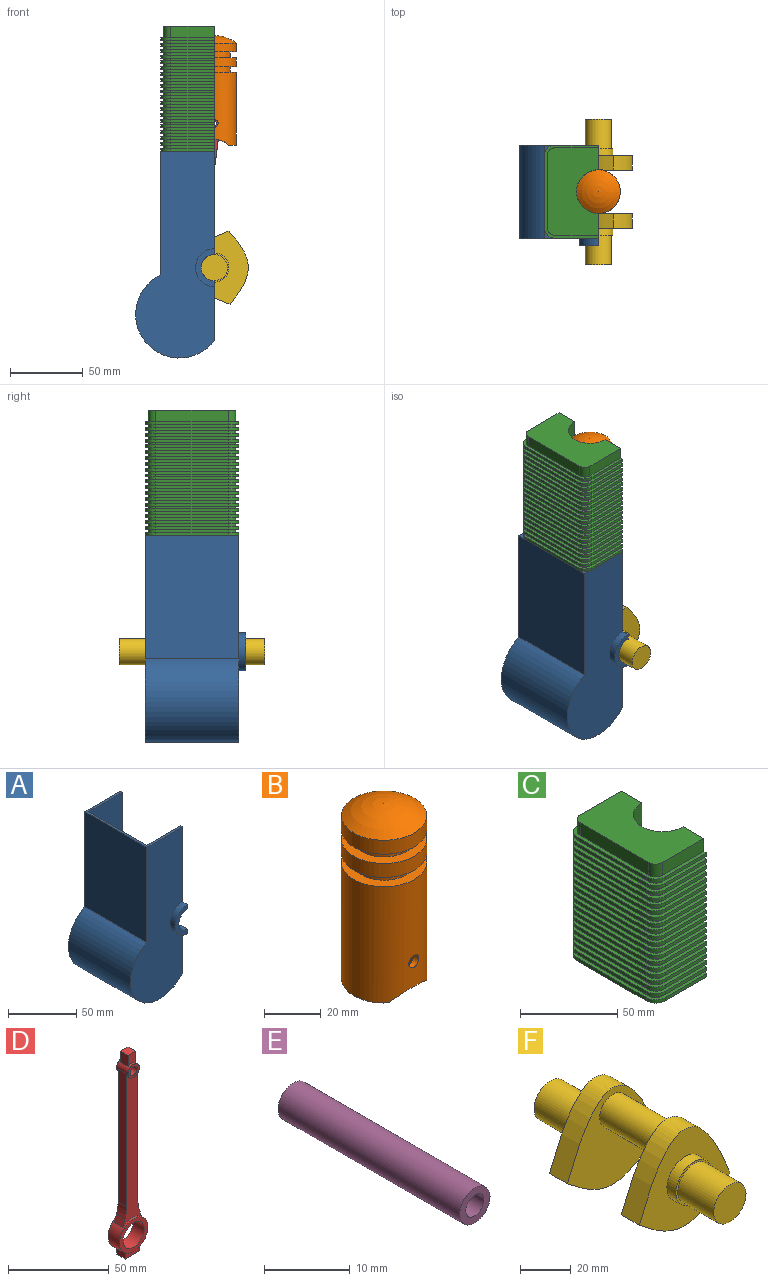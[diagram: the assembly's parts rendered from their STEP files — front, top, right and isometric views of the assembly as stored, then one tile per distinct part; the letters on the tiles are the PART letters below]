
ASSEMBLY  parts=6 mates=4
PART A: 16 faces, bbox 54.1x69x142.1 mm
  f0: plane 71x2mm, normal (1,0,0), area 142mm2, adj f2,f7,f11,f12
  f1: plane 71x7mm, normal (1,0,0), area 162mm2, adj f2,f6,f10,f13,f14,f15
  f2: plane 64x37mm, normal (0,0,1), area 268mm2, adj f0,f1,f5,f6,f7,f9,f10,f11
  f3: plane 69x41mm, normal (1,0,0), area 400.2mm2, adj f4,f6,f7,f8,f10,f11,f12,f13
  f4: cylinder r=30mm len=64mm, axis (0,1,0), area 6965.7mm2, adj f3,f5,f6,f7
  f5: plane 85.03x64mm, normal (-1,0,0), area 5441.9mm2, adj f2,f4,f6,f7
  f6: plane 142.11x54.08mm, normal (0,-1,0), area 5555.5mm2, adj f1,f2,f3,f4,f5,f14
  f7: plane 142.11x54.08mm, normal (0,1,0), area 5693.7mm2, adj f0,f2,f3,f4,f5,f12
  f8: cylinder r=28mm len=60mm, axis (0,1,0), area 6343.8mm2, adj f3,f9,f10,f11
  f9: plane 86.32x60mm, normal (1,0,0), area 5179.4mm2, adj f2,f8,f10,f11
  f10: plane 140.11x52.08mm, normal (0,1,0), area 5307.9mm2, adj f1,f2,f3,f8,f9,f13
  f11: plane 140.11x52.08mm, normal (0,-1,0), area 5307.9mm2, adj f0,f2,f3,f8,f9,f12
  f12: cylinder r=9mm len=18mm, axis (0,-1,0), area 56.5mm2, adj f0,f3,f7,f11
  f13: cylinder r=9mm len=18mm, axis (0,-1,0), area 197.9mm2, adj f1,f3,f10,f15
  f14: cylinder r=13mm len=26mm, axis (0,1,0), area 204.2mm2, adj f1,f3,f6,f15
  f15: plane 26x13mm, normal (0,-1,0), area 138.2mm2, adj f1,f3,f13,f14
PART B: 26 faces, bbox 30x30x75.2 mm
  f0: plane 23.31x5.56mm, normal (0,0,-1), area 55.9mm2, adj f1,f2,f24,f25
  f1: cylinder r=15mm len=50mm, axis (0,0,1), area 4562mm2, adj f0,f3,f4,f22,f23,f24,f25
  f2: cylinder r=12.5mm len=47.5mm, axis (0,0,1), area 3577.3mm2, adj f0,f4,f13,f22,f23,f24,f25
  f3: plane 30x30mm, normal (0,0,1), area 326.7mm2, adj f1,f12
  f4: plane 23.31x5.56mm, normal (0,0,-1), area 55.9mm2, adj f1,f2,f24,f25
  f5: sphere r=24.12mm, area 792.9mm2, adj f6
  f6: cylinder r=15mm len=30mm, axis (0,0,1), area 565.5mm2, adj f5,f7
  f7: plane 30x30mm, normal (0,0,-1), area 326.7mm2, adj f6,f8
  f8: cylinder r=11mm len=22mm, axis (0,0,1), area 276.5mm2, adj f7,f9
  f9: plane 30x30mm, normal (0,0,1), area 326.7mm2, adj f8,f10
  f10: cylinder r=15mm len=30mm, axis (0,0,1), area 565.5mm2, adj f9,f11
  f11: plane 30x30mm, normal (0,0,-1), area 326.7mm2, adj f10,f12
  f12: cylinder r=11mm len=22mm, axis (0,0,1), area 276.5mm2, adj f3,f11
  f13: plane 25x25mm, normal (0,0,-1), area 263.9mm2, adj f2,f21
  f14: sphere r=21.62mm, area 540.7mm2, adj f15
  f15: cylinder r=12.5mm len=25mm, axis (0,0,1), area 176.9mm2, adj f14,f16
  f16: plane 25x25mm, normal (0,0,1), area 263.9mm2, adj f15,f17
  f17: cylinder r=8.5mm len=17mm, axis (0,0,1), area 480.7mm2, adj f16,f18
  f18: plane 25x25mm, normal (0,0,-1), area 263.9mm2, adj f17,f19
  f19: cylinder r=12.5mm len=25mm, axis (0,0,1), area 78.5mm2, adj f18,f20
  f20: plane 25x25mm, normal (0,0,1), area 263.9mm2, adj f19,f21
  f21: cylinder r=8.5mm len=17mm, axis (0,0,1), area 480.7mm2, adj f13,f20
  f22: cylinder r=2.5mm len=5mm, axis (0,1,0), area 39.6mm2, adj f1,f2
  f23: cylinder r=2.5mm len=5mm, axis (0,1,0), area 39.6mm2, adj f1,f2
  f24: cylinder r=13mm len=18.89mm, axis (0,-1,0), area 59mm2, adj f0,f1,f2,f4
  f25: cylinder r=13mm len=18.89mm, axis (0,-1,0), area 59mm2, adj f0,f1,f2,f4
PART C: 244 faces, bbox 37x64x86 mm
  f0: cylinder r=15mm len=86mm, axis (0,0,-1), area 4052.7mm2, adj f1,f7,f8,f231
  f1: plane 86x17mm, normal (1,0,0), area 1370mm2, adj f0,f2,f8,f10,f14,f15,f16,f22
  f2: plane 30x2mm, normal (0,1,0), area 60mm2, adj f1,f3,f14,f237
  f3: cylinder r=5mm len=5mm, axis (0,0,-1), area 15.7mm2, adj f2,f4,f14,f237
  f4: plane 50x2mm, normal (-1,0,0), area 100mm2, adj f3,f5,f14,f237
  f5: cylinder r=5mm len=5mm, axis (0,0,-1), area 15.7mm2, adj f4,f6,f14,f237
  f6: plane 30x2mm, normal (0,-1,0), area 60mm2, adj f5,f7,f14,f237
  f7: plane 86x17mm, normal (1,0,0), area 1370mm2, adj f0,f6,f8,f9,f14,f15,f20,f21
  f8: plane 64x37mm, normal (0,0,-1), area 1993.5mm2, adj f0,f1,f7,f9,f10,f11,f12,f13
  f9: plane 30x2mm, normal (0,-1,0), area 60mm2, adj f7,f8,f13,f14
  f10: plane 30x2mm, normal (0,1,0), area 60mm2, adj f1,f8,f11,f14
  f11: cylinder r=7mm len=7mm, axis (0,0,-1), area 22mm2, adj f8,f10,f12,f14
  f12: plane 50x2mm, normal (-1,0,0), area 100mm2, adj f8,f11,f13,f14
  f13: cylinder r=7mm len=7mm, axis (0,0,-1), area 22mm2, adj f8,f9,f12,f14
  f14: plane 64x37mm, normal (0,0,1), area 257.7mm2, adj f1,f2,f3,f4,f5,f6,f7,f9
  f15: plane 64x37mm, normal (0,0,-1), area 257.7mm2, adj f1,f7,f21,f22,f23,f24,f25,f232
  f16: plane 30x2mm, normal (0,1,0), area 60mm2, adj f1,f17,f26,f32
  f17: cylinder r=5mm len=5mm, axis (0,0,-1), area 15.7mm2, adj f16,f18,f26,f32
  f18: plane 50x2mm, normal (-1,0,0), area 100mm2, adj f17,f19,f26,f32
  f19: cylinder r=5mm len=5mm, axis (0,0,-1), area 15.7mm2, adj f18,f20,f26,f32
  f20: plane 30x2mm, normal (0,-1,0), area 60mm2, adj f7,f19,f26,f32
  f21: plane 30x2mm, normal (0,-1,0), area 60mm2, adj f7,f15,f25,f26
  f22: plane 30x2mm, normal (0,1,0), area 60mm2, adj f1,f15,f23,f26
  f23: cylinder r=7mm len=7mm, axis (0,0,-1), area 22mm2, adj f15,f22,f24,f26
  f24: plane 50x2mm, normal (-1,0,0), area 100mm2, adj f15,f23,f25,f26
  f25: cylinder r=7mm len=7mm, axis (0,0,-1), area 22mm2, adj f15,f21,f24,f26
  f26: plane 64x37mm, normal (0,0,1), area 257.7mm2, adj f1,f7,f16,f17,f18,f19,f20,f21
  f27: plane 30x2mm, normal (0,1,0), area 60mm2, adj f1,f28,f38,f44
  f28: cylinder r=5mm len=5mm, axis (0,0,-1), area 15.7mm2, adj f27,f29,f38,f44
  f29: plane 50x2mm, normal (-1,0,0), area 100mm2, adj f28,f30,f38,f44
  f30: cylinder r=5mm len=5mm, axis (0,0,-1), area 15.7mm2, adj f29,f31,f38,f44
  f31: plane 30x2mm, normal (0,-1,0), area 60mm2, adj f7,f30,f38,f44
  f32: plane 64x37mm, normal (0,0,-1), area 257.7mm2, adj f1,f7,f16,f17,f18,f19,f20,f33
  f33: plane 30x2mm, normal (0,-1,0), area 60mm2, adj f7,f32,f37,f38
  f34: plane 30x2mm, normal (0,1,0), area 60mm2, adj f1,f32,f35,f38
  f35: cylinder r=7mm len=7mm, axis (0,0,-1), area 22mm2, adj f32,f34,f36,f38
  f36: plane 50x2mm, normal (-1,0,0), area 100mm2, adj f32,f35,f37,f38
  f37: cylinder r=7mm len=7mm, axis (0,0,-1), area 22mm2, adj f32,f33,f36,f38
  f38: plane 64x37mm, normal (0,0,1), area 257.7mm2, adj f1,f7,f27,f28,f29,f30,f31,f33
  f39: plane 30x2mm, normal (0,1,0), area 60mm2, adj f1,f40,f50,f56
  f40: cylinder r=5mm len=5mm, axis (0,0,-1), area 15.7mm2, adj f39,f41,f50,f56
  f41: plane 50x2mm, normal (-1,0,0), area 100mm2, adj f40,f42,f50,f56
  f42: cylinder r=5mm len=5mm, axis (0,0,-1), area 15.7mm2, adj f41,f43,f50,f56
  f43: plane 30x2mm, normal (0,-1,0), area 60mm2, adj f7,f42,f50,f56
  f44: plane 64x37mm, normal (0,0,-1), area 257.7mm2, adj f1,f7,f27,f28,f29,f30,f31,f45
  f45: plane 30x2mm, normal (0,-1,0), area 60mm2, adj f7,f44,f49,f50
  f46: plane 30x2mm, normal (0,1,0), area 60mm2, adj f1,f44,f47,f50
  f47: cylinder r=7mm len=7mm, axis (0,0,-1), area 22mm2, adj f44,f46,f48,f50
  f48: plane 50x2mm, normal (-1,0,0), area 100mm2, adj f44,f47,f49,f50
  f49: cylinder r=7mm len=7mm, axis (0,0,-1), area 22mm2, adj f44,f45,f48,f50
  f50: plane 64x37mm, normal (0,0,1), area 257.7mm2, adj f1,f7,f39,f40,f41,f42,f43,f45
  f51: plane 30x2mm, normal (0,1,0), area 60mm2, adj f1,f52,f62,f68
  f52: cylinder r=5mm len=5mm, axis (0,0,-1), area 15.7mm2, adj f51,f53,f62,f68
  f53: plane 50x2mm, normal (-1,0,0), area 100mm2, adj f52,f54,f62,f68
  f54: cylinder r=5mm len=5mm, axis (0,0,-1), area 15.7mm2, adj f53,f55,f62,f68
  f55: plane 30x2mm, normal (0,-1,0), area 60mm2, adj f7,f54,f62,f68
  f56: plane 64x37mm, normal (0,0,-1), area 257.7mm2, adj f1,f7,f39,f40,f41,f42,f43,f57
  f57: plane 30x2mm, normal (0,-1,0), area 60mm2, adj f7,f56,f61,f62
  f58: plane 30x2mm, normal (0,1,0), area 60mm2, adj f1,f56,f59,f62
  f59: cylinder r=7mm len=7mm, axis (0,0,-1), area 22mm2, adj f56,f58,f60,f62
  f60: plane 50x2mm, normal (-1,0,0), area 100mm2, adj f56,f59,f61,f62
  f61: cylinder r=7mm len=7mm, axis (0,0,-1), area 22mm2, adj f56,f57,f60,f62
  f62: plane 64x37mm, normal (0,0,1), area 257.7mm2, adj f1,f7,f51,f52,f53,f54,f55,f57
  f63: plane 30x2mm, normal (0,1,0), area 60mm2, adj f1,f64,f74,f80
  f64: cylinder r=5mm len=5mm, axis (0,0,-1), area 15.7mm2, adj f63,f65,f74,f80
  f65: plane 50x2mm, normal (-1,0,0), area 100mm2, adj f64,f66,f74,f80
  f66: cylinder r=5mm len=5mm, axis (0,0,-1), area 15.7mm2, adj f65,f67,f74,f80
  f67: plane 30x2mm, normal (0,-1,0), area 60mm2, adj f7,f66,f74,f80
  f68: plane 64x37mm, normal (0,0,-1), area 257.7mm2, adj f1,f7,f51,f52,f53,f54,f55,f69
  f69: plane 30x2mm, normal (0,-1,0), area 60mm2, adj f7,f68,f73,f74
  f70: plane 30x2mm, normal (0,1,0), area 60mm2, adj f1,f68,f71,f74
  f71: cylinder r=7mm len=7mm, axis (0,0,-1), area 22mm2, adj f68,f70,f72,f74
  f72: plane 50x2mm, normal (-1,0,0), area 100mm2, adj f68,f71,f73,f74
  f73: cylinder r=7mm len=7mm, axis (0,0,-1), area 22mm2, adj f68,f69,f72,f74
  f74: plane 64x37mm, normal (0,0,1), area 257.7mm2, adj f1,f7,f63,f64,f65,f66,f67,f69
  f75: plane 30x2mm, normal (0,1,0), area 60mm2, adj f1,f76,f86,f92
  f76: cylinder r=5mm len=5mm, axis (0,0,-1), area 15.7mm2, adj f75,f77,f86,f92
  f77: plane 50x2mm, normal (-1,0,0), area 100mm2, adj f76,f78,f86,f92
  f78: cylinder r=5mm len=5mm, axis (0,0,-1), area 15.7mm2, adj f77,f79,f86,f92
  f79: plane 30x2mm, normal (0,-1,0), area 60mm2, adj f7,f78,f86,f92
  f80: plane 64x37mm, normal (0,0,-1), area 257.7mm2, adj f1,f7,f63,f64,f65,f66,f67,f81
  f81: plane 30x2mm, normal (0,-1,0), area 60mm2, adj f7,f80,f85,f86
  f82: plane 30x2mm, normal (0,1,0), area 60mm2, adj f1,f80,f83,f86
  f83: cylinder r=7mm len=7mm, axis (0,0,-1), area 22mm2, adj f80,f82,f84,f86
  f84: plane 50x2mm, normal (-1,0,0), area 100mm2, adj f80,f83,f85,f86
  f85: cylinder r=7mm len=7mm, axis (0,0,-1), area 22mm2, adj f80,f81,f84,f86
  f86: plane 64x37mm, normal (0,0,1), area 257.7mm2, adj f1,f7,f75,f76,f77,f78,f79,f81
  f87: plane 30x2mm, normal (0,1,0), area 60mm2, adj f1,f88,f98,f104
  f88: cylinder r=5mm len=5mm, axis (0,0,-1), area 15.7mm2, adj f87,f89,f98,f104
  f89: plane 50x2mm, normal (-1,0,0), area 100mm2, adj f88,f90,f98,f104
  f90: cylinder r=5mm len=5mm, axis (0,0,-1), area 15.7mm2, adj f89,f91,f98,f104
  f91: plane 30x2mm, normal (0,-1,0), area 60mm2, adj f7,f90,f98,f104
  f92: plane 64x37mm, normal (0,0,-1), area 257.7mm2, adj f1,f7,f75,f76,f77,f78,f79,f93
  f93: plane 30x2mm, normal (0,-1,0), area 60mm2, adj f7,f92,f97,f98
  f94: plane 30x2mm, normal (0,1,0), area 60mm2, adj f1,f92,f95,f98
  f95: cylinder r=7mm len=7mm, axis (0,0,-1), area 22mm2, adj f92,f94,f96,f98
  f96: plane 50x2mm, normal (-1,0,0), area 100mm2, adj f92,f95,f97,f98
  f97: cylinder r=7mm len=7mm, axis (0,0,-1), area 22mm2, adj f92,f93,f96,f98
  f98: plane 64x37mm, normal (0,0,1), area 257.7mm2, adj f1,f7,f87,f88,f89,f90,f91,f93
  f99: plane 30x2mm, normal (0,1,0), area 60mm2, adj f1,f100,f110,f116
  f100: cylinder r=5mm len=5mm, axis (0,0,-1), area 15.7mm2, adj f99,f101,f110,f116
  f101: plane 50x2mm, normal (-1,0,0), area 100mm2, adj f100,f102,f110,f116
  f102: cylinder r=5mm len=5mm, axis (0,0,-1), area 15.7mm2, adj f101,f103,f110,f116
  f103: plane 30x2mm, normal (0,-1,0), area 60mm2, adj f7,f102,f110,f116
  f104: plane 64x37mm, normal (0,0,-1), area 257.7mm2, adj f1,f7,f87,f88,f89,f90,f91,f105
  f105: plane 30x2mm, normal (0,-1,0), area 60mm2, adj f7,f104,f109,f110
  f106: plane 30x2mm, normal (0,1,0), area 60mm2, adj f1,f104,f107,f110
  f107: cylinder r=7mm len=7mm, axis (0,0,-1), area 22mm2, adj f104,f106,f108,f110
  f108: plane 50x2mm, normal (-1,0,0), area 100mm2, adj f104,f107,f109,f110
  f109: cylinder r=7mm len=7mm, axis (0,0,-1), area 22mm2, adj f104,f105,f108,f110
  f110: plane 64x37mm, normal (0,0,1), area 257.7mm2, adj f1,f7,f99,f100,f101,f102,f103,f105
  f111: plane 30x2mm, normal (0,1,0), area 60mm2, adj f1,f112,f122,f128
  f112: cylinder r=5mm len=5mm, axis (0,0,-1), area 15.7mm2, adj f111,f113,f122,f128
  f113: plane 50x2mm, normal (-1,0,0), area 100mm2, adj f112,f114,f122,f128
  f114: cylinder r=5mm len=5mm, axis (0,0,-1), area 15.7mm2, adj f113,f115,f122,f128
  f115: plane 30x2mm, normal (0,-1,0), area 60mm2, adj f7,f114,f122,f128
  f116: plane 64x37mm, normal (0,0,-1), area 257.7mm2, adj f1,f7,f99,f100,f101,f102,f103,f117
  f117: plane 30x2mm, normal (0,-1,0), area 60mm2, adj f7,f116,f121,f122
  f118: plane 30x2mm, normal (0,1,0), area 60mm2, adj f1,f116,f119,f122
  f119: cylinder r=7mm len=7mm, axis (0,0,-1), area 22mm2, adj f116,f118,f120,f122
  f120: plane 50x2mm, normal (-1,0,0), area 100mm2, adj f116,f119,f121,f122
  f121: cylinder r=7mm len=7mm, axis (0,0,-1), area 22mm2, adj f116,f117,f120,f122
  f122: plane 64x37mm, normal (0,0,1), area 257.7mm2, adj f1,f7,f111,f112,f113,f114,f115,f117
  f123: plane 30x2mm, normal (0,1,0), area 60mm2, adj f1,f124,f134,f140
  f124: cylinder r=5mm len=5mm, axis (0,0,-1), area 15.7mm2, adj f123,f125,f134,f140
  f125: plane 50x2mm, normal (-1,0,0), area 100mm2, adj f124,f126,f134,f140
  f126: cylinder r=5mm len=5mm, axis (0,0,-1), area 15.7mm2, adj f125,f127,f134,f140
  f127: plane 30x2mm, normal (0,-1,0), area 60mm2, adj f7,f126,f134,f140
  f128: plane 64x37mm, normal (0,0,-1), area 257.7mm2, adj f1,f7,f111,f112,f113,f114,f115,f129
  f129: plane 30x2mm, normal (0,-1,0), area 60mm2, adj f7,f128,f133,f134
  f130: plane 30x2mm, normal (0,1,0), area 60mm2, adj f1,f128,f131,f134
  f131: cylinder r=7mm len=7mm, axis (0,0,-1), area 22mm2, adj f128,f130,f132,f134
  f132: plane 50x2mm, normal (-1,0,0), area 100mm2, adj f128,f131,f133,f134
  f133: cylinder r=7mm len=7mm, axis (0,0,-1), area 22mm2, adj f128,f129,f132,f134
  f134: plane 64x37mm, normal (0,0,1), area 257.7mm2, adj f1,f7,f123,f124,f125,f126,f127,f129
  f135: plane 30x2mm, normal (0,1,0), area 60mm2, adj f1,f136,f146,f152
  f136: cylinder r=5mm len=5mm, axis (0,0,-1), area 15.7mm2, adj f135,f137,f146,f152
  f137: plane 50x2mm, normal (-1,0,0), area 100mm2, adj f136,f138,f146,f152
  f138: cylinder r=5mm len=5mm, axis (0,0,-1), area 15.7mm2, adj f137,f139,f146,f152
  f139: plane 30x2mm, normal (0,-1,0), area 60mm2, adj f7,f138,f146,f152
  f140: plane 64x37mm, normal (0,0,-1), area 257.7mm2, adj f1,f7,f123,f124,f125,f126,f127,f141
  f141: plane 30x2mm, normal (0,-1,0), area 60mm2, adj f7,f140,f145,f146
  f142: plane 30x2mm, normal (0,1,0), area 60mm2, adj f1,f140,f143,f146
  f143: cylinder r=7mm len=7mm, axis (0,0,-1), area 22mm2, adj f140,f142,f144,f146
  f144: plane 50x2mm, normal (-1,0,0), area 100mm2, adj f140,f143,f145,f146
  f145: cylinder r=7mm len=7mm, axis (0,0,-1), area 22mm2, adj f140,f141,f144,f146
  f146: plane 64x37mm, normal (0,0,1), area 257.7mm2, adj f1,f7,f135,f136,f137,f138,f139,f141
  f147: plane 30x2mm, normal (0,1,0), area 60mm2, adj f1,f148,f158,f164
  f148: cylinder r=5mm len=5mm, axis (0,0,-1), area 15.7mm2, adj f147,f149,f158,f164
  f149: plane 50x2mm, normal (-1,0,0), area 100mm2, adj f148,f150,f158,f164
  f150: cylinder r=5mm len=5mm, axis (0,0,-1), area 15.7mm2, adj f149,f151,f158,f164
  f151: plane 30x2mm, normal (0,-1,0), area 60mm2, adj f7,f150,f158,f164
  f152: plane 64x37mm, normal (0,0,-1), area 257.7mm2, adj f1,f7,f135,f136,f137,f138,f139,f153
  f153: plane 30x2mm, normal (0,-1,0), area 60mm2, adj f7,f152,f157,f158
  f154: plane 30x2mm, normal (0,1,0), area 60mm2, adj f1,f152,f155,f158
  f155: cylinder r=7mm len=7mm, axis (0,0,-1), area 22mm2, adj f152,f154,f156,f158
  f156: plane 50x2mm, normal (-1,0,0), area 100mm2, adj f152,f155,f157,f158
  f157: cylinder r=7mm len=7mm, axis (0,0,-1), area 22mm2, adj f152,f153,f156,f158
  f158: plane 64x37mm, normal (0,0,1), area 257.7mm2, adj f1,f7,f147,f148,f149,f150,f151,f153
  f159: plane 30x2mm, normal (0,1,0), area 60mm2, adj f1,f160,f170,f176
  f160: cylinder r=5mm len=5mm, axis (0,0,-1), area 15.7mm2, adj f159,f161,f170,f176
  f161: plane 50x2mm, normal (-1,0,0), area 100mm2, adj f160,f162,f170,f176
  f162: cylinder r=5mm len=5mm, axis (0,0,-1), area 15.7mm2, adj f161,f163,f170,f176
  f163: plane 30x2mm, normal (0,-1,0), area 60mm2, adj f7,f162,f170,f176
  f164: plane 64x37mm, normal (0,0,-1), area 257.7mm2, adj f1,f7,f147,f148,f149,f150,f151,f165
  f165: plane 30x2mm, normal (0,-1,0), area 60mm2, adj f7,f164,f169,f170
  f166: plane 30x2mm, normal (0,1,0), area 60mm2, adj f1,f164,f167,f170
  f167: cylinder r=7mm len=7mm, axis (0,0,-1), area 22mm2, adj f164,f166,f168,f170
  f168: plane 50x2mm, normal (-1,0,0), area 100mm2, adj f164,f167,f169,f170
  f169: cylinder r=7mm len=7mm, axis (0,0,-1), area 22mm2, adj f164,f165,f168,f170
  f170: plane 64x37mm, normal (0,0,1), area 257.7mm2, adj f1,f7,f159,f160,f161,f162,f163,f165
  f171: plane 30x2mm, normal (0,1,0), area 60mm2, adj f1,f172,f182,f188
  f172: cylinder r=5mm len=5mm, axis (0,0,-1), area 15.7mm2, adj f171,f173,f182,f188
  f173: plane 50x2mm, normal (-1,0,0), area 100mm2, adj f172,f174,f182,f188
  f174: cylinder r=5mm len=5mm, axis (0,0,-1), area 15.7mm2, adj f173,f175,f182,f188
  f175: plane 30x2mm, normal (0,-1,0), area 60mm2, adj f7,f174,f182,f188
  f176: plane 64x37mm, normal (0,0,-1), area 257.7mm2, adj f1,f7,f159,f160,f161,f162,f163,f177
  f177: plane 30x2mm, normal (0,-1,0), area 60mm2, adj f7,f176,f181,f182
  f178: plane 30x2mm, normal (0,1,0), area 60mm2, adj f1,f176,f179,f182
  f179: cylinder r=7mm len=7mm, axis (0,0,-1), area 22mm2, adj f176,f178,f180,f182
  f180: plane 50x2mm, normal (-1,0,0), area 100mm2, adj f176,f179,f181,f182
  f181: cylinder r=7mm len=7mm, axis (0,0,-1), area 22mm2, adj f176,f177,f180,f182
  f182: plane 64x37mm, normal (0,0,1), area 257.7mm2, adj f1,f7,f171,f172,f173,f174,f175,f177
  f183: plane 30x2mm, normal (0,1,0), area 60mm2, adj f1,f184,f194,f200
  f184: cylinder r=5mm len=5mm, axis (0,0,-1), area 15.7mm2, adj f183,f185,f194,f200
  f185: plane 50x2mm, normal (-1,0,0), area 100mm2, adj f184,f186,f194,f200
  f186: cylinder r=5mm len=5mm, axis (0,0,-1), area 15.7mm2, adj f185,f187,f194,f200
  f187: plane 30x2mm, normal (0,-1,0), area 60mm2, adj f7,f186,f194,f200
  f188: plane 64x37mm, normal (0,0,-1), area 257.7mm2, adj f1,f7,f171,f172,f173,f174,f175,f189
  f189: plane 30x2mm, normal (0,-1,0), area 60mm2, adj f7,f188,f193,f194
  f190: plane 30x2mm, normal (0,1,0), area 60mm2, adj f1,f188,f191,f194
  f191: cylinder r=7mm len=7mm, axis (0,0,-1), area 22mm2, adj f188,f190,f192,f194
  f192: plane 50x2mm, normal (-1,0,0), area 100mm2, adj f188,f191,f193,f194
  f193: cylinder r=7mm len=7mm, axis (0,0,-1), area 22mm2, adj f188,f189,f192,f194
  f194: plane 64x37mm, normal (0,0,1), area 257.7mm2, adj f1,f7,f183,f184,f185,f186,f187,f189
  f195: plane 30x2mm, normal (0,1,0), area 60mm2, adj f1,f196,f206,f212
  f196: cylinder r=5mm len=5mm, axis (0,0,-1), area 15.7mm2, adj f195,f197,f206,f212
  f197: plane 50x2mm, normal (-1,0,0), area 100mm2, adj f196,f198,f206,f212
  f198: cylinder r=5mm len=5mm, axis (0,0,-1), area 15.7mm2, adj f197,f199,f206,f212
  f199: plane 30x2mm, normal (0,-1,0), area 60mm2, adj f7,f198,f206,f212
  f200: plane 64x37mm, normal (0,0,-1), area 257.7mm2, adj f1,f7,f183,f184,f185,f186,f187,f201
  f201: plane 30x2mm, normal (0,-1,0), area 60mm2, adj f7,f200,f205,f206
  f202: plane 30x2mm, normal (0,1,0), area 60mm2, adj f1,f200,f203,f206
  f203: cylinder r=7mm len=7mm, axis (0,0,-1), area 22mm2, adj f200,f202,f204,f206
  f204: plane 50x2mm, normal (-1,0,0), area 100mm2, adj f200,f203,f205,f206
  f205: cylinder r=7mm len=7mm, axis (0,0,-1), area 22mm2, adj f200,f201,f204,f206
  f206: plane 64x37mm, normal (0,0,1), area 257.7mm2, adj f1,f7,f195,f196,f197,f198,f199,f201
  f207: plane 30x2mm, normal (0,1,0), area 60mm2, adj f1,f208,f218,f224
  f208: cylinder r=5mm len=5mm, axis (0,0,-1), area 15.7mm2, adj f207,f209,f218,f224
  f209: plane 50x2mm, normal (-1,0,0), area 100mm2, adj f208,f210,f218,f224
  f210: cylinder r=5mm len=5mm, axis (0,0,-1), area 15.7mm2, adj f209,f211,f218,f224
  f211: plane 30x2mm, normal (0,-1,0), area 60mm2, adj f7,f210,f218,f224
  f212: plane 64x37mm, normal (0,0,-1), area 257.7mm2, adj f1,f7,f195,f196,f197,f198,f199,f213
  f213: plane 30x2mm, normal (0,-1,0), area 60mm2, adj f7,f212,f217,f218
  f214: plane 30x2mm, normal (0,1,0), area 60mm2, adj f1,f212,f215,f218
  f215: cylinder r=7mm len=7mm, axis (0,0,-1), area 22mm2, adj f212,f214,f216,f218
  f216: plane 50x2mm, normal (-1,0,0), area 100mm2, adj f212,f215,f217,f218
  f217: cylinder r=7mm len=7mm, axis (0,0,-1), area 22mm2, adj f212,f213,f216,f218
  f218: plane 64x37mm, normal (0,0,1), area 257.7mm2, adj f1,f7,f207,f208,f209,f210,f211,f213
  f219: plane 30x8mm, normal (0,1,0), area 240mm2, adj f1,f220,f230,f231
  f220: cylinder r=5mm len=8mm, axis (0,0,-1), area 62.8mm2, adj f219,f221,f230,f231
  f221: plane 50x8mm, normal (-1,0,0), area 400mm2, adj f220,f222,f230,f231
  f222: cylinder r=5mm len=8mm, axis (0,0,-1), area 62.8mm2, adj f221,f223,f230,f231
  f223: plane 30x8mm, normal (0,-1,0), area 240mm2, adj f7,f222,f230,f231
  f224: plane 64x37mm, normal (0,0,-1), area 257.7mm2, adj f1,f7,f207,f208,f209,f210,f211,f225
  f225: plane 30x2mm, normal (0,-1,0), area 60mm2, adj f7,f224,f229,f230
  f226: plane 30x2mm, normal (0,1,0), area 60mm2, adj f1,f224,f227,f230
  f227: cylinder r=7mm len=7mm, axis (0,0,-1), area 22mm2, adj f224,f226,f228,f230
  f228: plane 50x2mm, normal (-1,0,0), area 100mm2, adj f224,f227,f229,f230
  f229: cylinder r=7mm len=7mm, axis (0,0,-1), area 22mm2, adj f224,f225,f228,f230
  f230: plane 64x37mm, normal (0,0,1), area 257.7mm2, adj f1,f7,f219,f220,f221,f222,f223,f225
  f231: plane 60x35mm, normal (0,0,1), area 1735.8mm2, adj f0,f1,f7,f219,f220,f221,f222,f223
  f232: plane 30x2mm, normal (0,1,0), area 60mm2, adj f1,f15,f233,f243
  f233: cylinder r=5mm len=5mm, axis (0,0,-1), area 15.7mm2, adj f15,f232,f234,f243
  f234: plane 50x2mm, normal (-1,0,0), area 100mm2, adj f15,f233,f235,f243
  f235: cylinder r=5mm len=5mm, axis (0,0,-1), area 15.7mm2, adj f15,f234,f236,f243
  f236: plane 30x2mm, normal (0,-1,0), area 60mm2, adj f7,f15,f235,f243
  f237: plane 64x37mm, normal (0,0,-1), area 257.7mm2, adj f1,f2,f3,f4,f5,f6,f7,f238
  f238: plane 30x2mm, normal (0,-1,0), area 60mm2, adj f7,f237,f242,f243
  f239: plane 30x2mm, normal (0,1,0), area 60mm2, adj f1,f237,f240,f243
  f240: cylinder r=7mm len=7mm, axis (0,0,-1), area 22mm2, adj f237,f239,f241,f243
  f241: plane 50x2mm, normal (-1,0,0), area 100mm2, adj f237,f240,f242,f243
  f242: cylinder r=7mm len=7mm, axis (0,0,-1), area 22mm2, adj f237,f238,f241,f243
  f243: plane 64x37mm, normal (0,0,1), area 257.7mm2, adj f1,f7,f232,f233,f234,f235,f236,f238
PART D: 31 faces, bbox 20x8x122.7 mm
  f0: cylinder r=20mm len=6.84mm, axis (0,1,0), area 30.3mm2, adj f1,f10,f14,f15,f21,f22,f23
  f1: plane 81.06x6mm, normal (1,0,0), area 430.7mm2, adj f0,f2,f14,f15,f22,f23,f24
  f2: cylinder r=4mm len=8mm, axis (0,1,0), area 104.5mm2, adj f1,f4,f5,f11,f14,f15,f27,f28
  f3: cylinder r=2.5mm len=8mm, axis (0,1,0), area 125.7mm2, adj f4,f5
  f4: plane 8x8mm, normal (0,-1,0), area 30.6mm2, adj f2,f3
  f5: plane 8x8mm, normal (0,1,0), area 30.6mm2, adj f2,f3
  f6: cylinder r=10mm len=20mm, axis (0,1,0), area 351.6mm2, adj f8,f9,f10,f13,f14,f15,f16,f17
  f7: cylinder r=7.5mm len=15mm, axis (0,1,0), area 377mm2, adj f8,f9
  f8: plane 20x20mm, normal (0,-1,0), area 137.4mm2, adj f6,f7
  f9: plane 20x20mm, normal (0,1,0), area 137.4mm2, adj f6,f7
  f10: plane 6x4.2mm, normal (0.94,0,0.34), area 26.8mm2, adj f0,f6,f14,f15
  f11: plane 81.06x6mm, normal (-1,0,0), area 486.3mm2, adj f2,f12,f14,f15
  f12: cylinder r=20mm len=6.84mm, axis (0,1,0), area 41.9mm2, adj f11,f13,f14,f15
  f13: plane 6x4.2mm, normal (-0.94,0,0.34), area 26.8mm2, adj f6,f12,f14,f15
  f14: plane 92.1x13.41mm, normal (0,-1,0), area 708.4mm2, adj f0,f1,f2,f6,f10,f11,f12,f13
  f15: plane 92.1x13.41mm, normal (0,1,0), area 708.4mm2, adj f0,f1,f2,f6,f10,f11,f12,f13
  f16: plane 6x4mm, normal (1,0,0), area 24mm2, adj f6,f18,f19,f20
  f17: plane 6x4mm, normal (-1,0,0), area 24mm2, adj f6,f18,f19,f20
  f18: plane 10x6mm, normal (0,0,-1), area 60mm2, adj f16,f17,f19,f20
  f19: plane 10x4mm, normal (0,-1,0), area 30.9mm2, adj f6,f16,f17,f18
  f20: plane 10x4mm, normal (0,1,0), area 30.9mm2, adj f6,f16,f17,f18
  f21: cylinder r=1.5mm len=3mm, axis (1,0,0), area 6.3mm2, adj f0,f22,f23,f25
  f22: plane 20x1.18mm, normal (0,1,0), area 20.2mm2, adj f0,f1,f21,f24,f25
  f23: plane 20x1.18mm, normal (0,-1,0), area 20.2mm2, adj f0,f1,f21,f24,f25
  f24: cylinder r=1.5mm len=3mm, axis (1,0,0), area 4.7mm2, adj f1,f22,f23,f25
  f25: plane 23x3mm, normal (1,0,0), area 67.1mm2, adj f21,f22,f23,f24
  f26: plane 5x5mm, normal (0,0,1), area 25mm2, adj f27,f28,f29,f30
  f27: plane 6.88x5mm, normal (-1,0,0), area 34.4mm2, adj f2,f26,f29,f30
  f28: plane 6.88x5mm, normal (1,0,0), area 34.4mm2, adj f2,f26,f29,f30
  f29: plane 6.88x5mm, normal (0,-1,0), area 31.4mm2, adj f2,f26,f27,f28
  f30: plane 6.88x5mm, normal (0,1,0), area 31.4mm2, adj f2,f26,f27,f28
PART E: 4 faces, bbox 5x30x5 mm
  f0: cylinder r=1.5mm len=30mm, axis (0,-1,0), area 282.7mm2, adj f2,f3
  f1: cylinder r=2.5mm len=30mm, axis (0,-1,0), area 471.2mm2, adj f2,f3
  f2: plane 5x5mm, normal (0,1,0), area 12.6mm2, adj f0,f1
  f3: plane 5x5mm, normal (0,-1,0), area 12.6mm2, adj f0,f1
PART F: 17 faces, bbox 50.4x100x65.5 mm
  f0: extruded ~50.42x33.65mm, area 880mm2, adj f1,f2,f3
  f1: extruded ~50.42x12.89mm, area 577.8mm2, adj f0,f2,f3
  f2: plane 65.52x50.42mm, normal (0,1,0), area 1369.6mm2, adj f0,f1,f8
  f3: plane 65.52x50.42mm, normal (0,-1,0), area 1232.2mm2, adj f0,f1,f4
  f4: cylinder r=10mm len=20mm, axis (0,1,0), area 314.2mm2, adj f3,f5
  f5: plane 20x20mm, normal (0,-1,0), area 59.7mm2, adj f4,f6
  f6: cylinder r=9mm len=20mm, axis (0,1,0), area 1131mm2, adj f5,f7
  f7: plane 18x18mm, normal (0,-1,0), area 254.5mm2, adj f6
  f8: cylinder r=7.5mm len=30mm, axis (0,-1,0), area 1413.7mm2, adj f2,f11
  f9: extruded ~50.42x33.65mm, area 880mm2, adj f10,f11,f12
  f10: extruded ~50.42x12.89mm, area 577.8mm2, adj f9,f11,f12
  f11: plane 65.52x50.42mm, normal (0,-1,0), area 1369.6mm2, adj f8,f9,f10
  f12: plane 65.52x50.42mm, normal (0,1,0), area 1232.2mm2, adj f9,f10,f13
  f13: cylinder r=10mm len=20mm, axis (0,-1,0), area 314.2mm2, adj f12,f14
  f14: plane 20x20mm, normal (0,1,0), area 59.7mm2, adj f13,f15
  f15: cylinder r=9mm len=20mm, axis (0,-1,0), area 1131mm2, adj f14,f16
  f16: plane 18x18mm, normal (0,1,0), area 254.5mm2, adj f15
PLACE A t=(-33.89,-45.8,-21.83)mm fixed
PLACE B t=(-48.89,-45.8,112.34)mm
PLACE C t=(-33.89,-45.8,184.17)mm fixed
PLACE D rot(axis=(0,1,0),7.2deg) t=(-46.39,-45.8,28)mm
PLACE E rot(axis=(0,1,0),7.2deg) t=(-33.89,-60.8,127.22)mm
PLACE F rot(axis=(0,-1,0),90.8deg) t=(-23.51,-70.8,28.31)mm
MATE revolute A.f12 <-> F.f4  axis (0,-1,0) through (-33.89,-75.8,28.17)mm
MATE fastened E.f1 <-> D.f2  axis (0,-1,0) through (-33.89,-45.8,127.22)mm
MATE slider C.f0 <-> B.f1  axis (0,0,-1) through (-33.89,-45.8,151.17)mm
MATE revolute F.f8 <-> D.f6  axis (0,-1,0) through (-46.39,-45.8,28)mm
